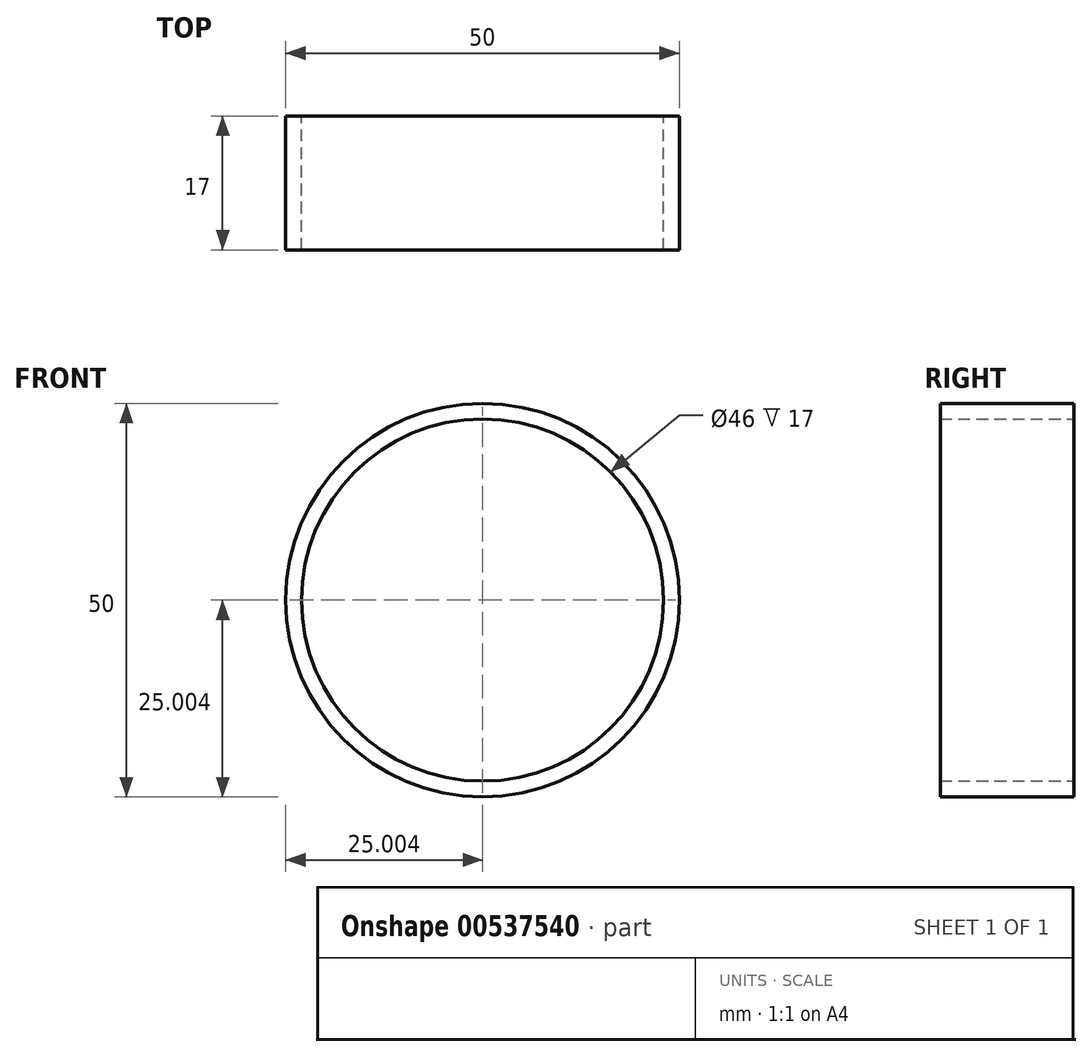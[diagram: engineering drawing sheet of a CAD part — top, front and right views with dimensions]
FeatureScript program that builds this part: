
annotation { "Feature Type Name" : "Feature", "Feature Type Description" : "" }
export const myFeature = defineFeature(function(context is Context, id is Id, definition is map)
    precondition{}
    {
        {
            var Q0;
            Q0=qCreatedBy(makeId("Front.planeOp"),FACE);
            var sketch = newSketch(context, id + "F0", { "sketchPlane" : qUnion([Q0])});
            skCircle(sketch, "E0", {"center": v(-42.59, 26) * mm, "radius": 25 * mm});
            skCircle(sketch, "E1", {"center": v(-42.59, 26) * mm, "radius": 23 * mm});
            skSolve(sketch);
        }
        {
            var Q0;
            Q0 = qSketchRegion(id + "F0", true);
            extrude(context, id + "F1", {"entities" : qUnion([Q0]), "depth" : 17 * mm, "offsetDistance" : 25 * mm});
        }
    });
